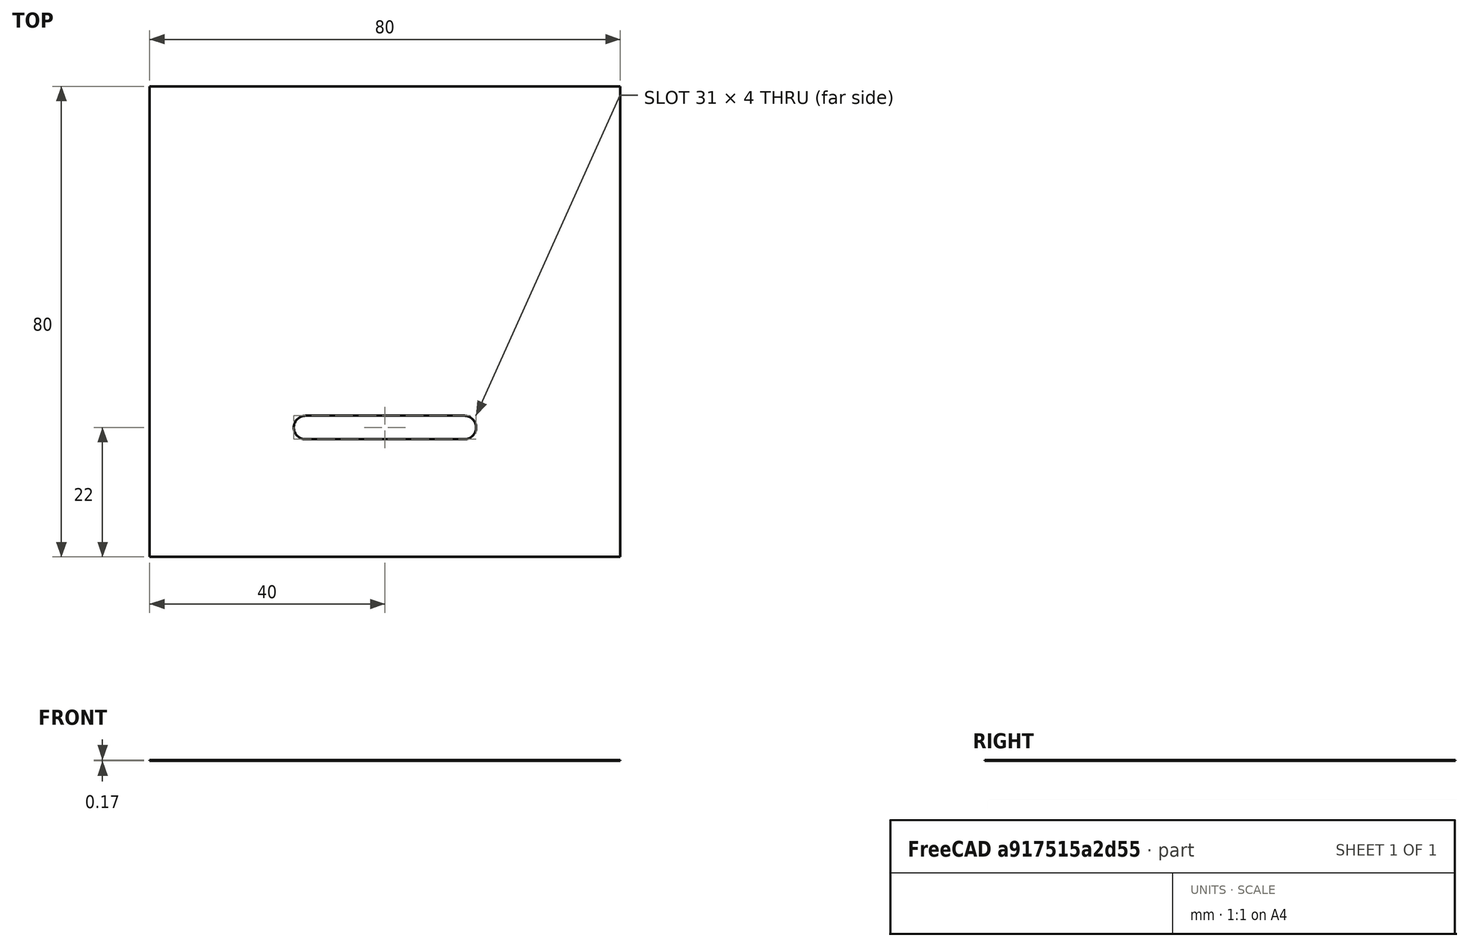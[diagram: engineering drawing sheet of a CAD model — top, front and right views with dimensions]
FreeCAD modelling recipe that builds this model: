
FCSTD DOCUMENT  (FreeCAD 0.19R24291 (Git))
Label: TopLabel
License: All rights reserved
LicenseURL: http://en.wikipedia.org/wiki/All_rights_reserved
objects: Part::Part2DObjectPython×3, Sketcher::SketchObject×2, Image::ImagePlane×1, PartDesign::Pad×1, PartDesign::Body×1
note: 8 computed .brp shape members not serialized (recipe doc carries the construction recipe); baked Part::Feature solids carry a one-line shape summary decoded from their .brp

FEATURE [Part::Part2DObjectPython] ShapeString  # Draft 2D object (typed FeaturePython)
  FontFile = <path>
  Placement = pos=(29.9,-64,0) rot=(0,0,1;0rad)
  Size = 3
  String = E0
  Tracking = 0
FEATURE [Part::Part2DObjectPython] ShapeString001  # Draft 2D object (typed FeaturePython)
  FontFile = <path>
  Placement = pos=(36.4,-64,0) rot=(0,0,1;0rad)
  Size = 3
  String = 2.4
  Tracking = 0
FEATURE [Part::Part2DObjectPython] ShapeString002  # Draft 2D object (typed FeaturePython)
  FontFile = <path>
  Placement = pos=(43.2,-64,0) rot=(0,0,1;0rad)
  Size = 3
  String = 5
  Tracking = 0
FEATURE [Sketcher::SketchObject] Sketch
  FullyConstrained = true
  MapMode = 5
  Support = -> [XY_Plane]
  sketch-geometry (9):
    g0: LineSegment StartX=0 StartY=0 StartZ=0 EndX=80 EndY=0 EndZ=0
    g1: LineSegment StartX=80 StartY=0 StartZ=0 EndX=80 EndY=-80 EndZ=0
    g2: LineSegment StartX=80 StartY=-80 StartZ=0 EndX=0 EndY=-80 EndZ=0
    g3: LineSegment StartX=0 StartY=-80 StartZ=0 EndX=0 EndY=0 EndZ=0
    g4: ArcOfCircle CenterX=26.5 CenterY=-58 CenterZ=0 NormalX=0 NormalY=0 NormalZ=1 AngleXU=0 Radius=2 StartAngle=1.5708 EndAngle=4.71239
    g5: ArcOfCircle CenterX=53.5 CenterY=-58 CenterZ=0 NormalX=0 NormalY=0 NormalZ=1 AngleXU=0 Radius=2 StartAngle=4.71239 EndAngle=7.85398
    g6: LineSegment StartX=26.5 StartY=-60 StartZ=0 EndX=53.5 EndY=-60 EndZ=0
    g7: LineSegment StartX=26.5 StartY=-56 StartZ=0 EndX=53.5 EndY=-56 EndZ=0
    g8: GeomPoint X=40 Y=-60 Z=0
  constraints (22):
    c: Coincident(g0,g1)
    c: Coincident(g1,g2)
    c: Coincident(g2,g3)
    c: Coincident(g3,g0)
    c: Horizontal(g0)
    c: Horizontal(g2)
    c: Vertical(g1)
    c: Vertical(g3)
    c: Coincident(g0,g-1)
    c: DistanceX(g0,g0) = 80
    c: DistanceY(g2,g0) = 80
    c: Tangent(g4,g7) = 1.5708
    c: Tangent(g4,g6) = -1.5708
    c: Tangent(g6,g5) = -1.5708
    c: Tangent(g7,g5) = 1.5708
    c: Horizontal(g6)
    c: Equal(g4,g5)
    c: DistanceY(g4,g4) = 4
    c: DistanceX(g4,g5) = 27
    c: Symmetric(g6,g6,g8)
    c: DistanceX(g0,g8) = 40
    c: DistanceY(g8,g0) = 60
FEATURE [Sketcher::SketchObject] MirroredSketch001
  FullyConstrained = false
  Placement = pos=(8,-51,0) rot=(0,0,1;0rad)
  sketch-geometry (86):
    g0: BSplineCurve PolesCount=2 KnotsCount=2 Degree=1 IsPeriodic=0
    g1: BSplineCurve PolesCount=2 KnotsCount=2 Degree=1 IsPeriodic=0
    g2: BSplineCurve PolesCount=2 KnotsCount=2 Degree=1 IsPeriodic=0
    g3: BSplineCurve PolesCount=4 KnotsCount=2 Degree=3 IsPeriodic=0
    g4: BSplineCurve PolesCount=2 KnotsCount=2 Degree=1 IsPeriodic=0
    g5: BSplineCurve PolesCount=4 KnotsCount=2 Degree=3 IsPeriodic=0
    g6: BSplineCurve PolesCount=2 KnotsCount=2 Degree=1 IsPeriodic=0
    g7: BSplineCurve PolesCount=4 KnotsCount=2 Degree=3 IsPeriodic=0
    g8: BSplineCurve PolesCount=2 KnotsCount=2 Degree=1 IsPeriodic=0
    g9: BSplineCurve PolesCount=4 KnotsCount=2 Degree=3 IsPeriodic=0
    g10: BSplineCurve PolesCount=2 KnotsCount=2 Degree=1 IsPeriodic=0
    g11: BSplineCurve PolesCount=2 KnotsCount=2 Degree=1 IsPeriodic=0
    g12: BSplineCurve PolesCount=2 KnotsCount=2 Degree=1 IsPeriodic=0
    g13: BSplineCurve PolesCount=4 KnotsCount=2 Degree=3 IsPeriodic=0
    g14: BSplineCurve PolesCount=4 KnotsCount=2 Degree=3 IsPeriodic=0
    g15: BSplineCurve PolesCount=2 KnotsCount=2 Degree=1 IsPeriodic=0
    g16: BSplineCurve PolesCount=2 KnotsCount=2 Degree=1 IsPeriodic=0
    g17: BSplineCurve PolesCount=2 KnotsCount=2 Degree=1 IsPeriodic=0
    g18: BSplineCurve PolesCount=4 KnotsCount=2 Degree=3 IsPeriodic=0
    g19: BSplineCurve PolesCount=2 KnotsCount=2 Degree=1 IsPeriodic=0
    g20: BSplineCurve PolesCount=4 KnotsCount=2 Degree=3 IsPeriodic=0
    g21: BSplineCurve PolesCount=2 KnotsCount=2 Degree=1 IsPeriodic=0
    g22: BSplineCurve PolesCount=4 KnotsCount=2 Degree=3 IsPeriodic=0
    g23: BSplineCurve PolesCount=2 KnotsCount=2 Degree=1 IsPeriodic=0
    g24: BSplineCurve PolesCount=4 KnotsCount=2 Degree=3 IsPeriodic=0
    g25: BSplineCurve PolesCount=2 KnotsCount=2 Degree=1 IsPeriodic=0
    g26: BSplineCurve PolesCount=2 KnotsCount=2 Degree=1 IsPeriodic=0
    g27: BSplineCurve PolesCount=2 KnotsCount=2 Degree=1 IsPeriodic=0
    g28: BSplineCurve PolesCount=2 KnotsCount=2 Degree=1 IsPeriodic=0
    g29: BSplineCurve PolesCount=2 KnotsCount=2 Degree=1 IsPeriodic=0
    g30: BSplineCurve PolesCount=4 KnotsCount=2 Degree=3 IsPeriodic=0
    g31: BSplineCurve PolesCount=2 KnotsCount=2 Degree=1 IsPeriodic=0
    g32: BSplineCurve PolesCount=4 KnotsCount=2 Degree=3 IsPeriodic=0
    g33: BSplineCurve PolesCount=2 KnotsCount=2 Degree=1 IsPeriodic=0
    g34: BSplineCurve PolesCount=4 KnotsCount=2 Degree=3 IsPeriodic=0
    g35: BSplineCurve PolesCount=2 KnotsCount=2 Degree=1 IsPeriodic=0
    g36: BSplineCurve PolesCount=4 KnotsCount=2 Degree=3 IsPeriodic=0
    g37: BSplineCurve PolesCount=2 KnotsCount=2 Degree=1 IsPeriodic=0
    g38: BSplineCurve PolesCount=2 KnotsCount=2 Degree=1 IsPeriodic=0
    g39: BSplineCurve PolesCount=2 KnotsCount=2 Degree=1 IsPeriodic=0
    g40: BSplineCurve PolesCount=4 KnotsCount=2 Degree=3 IsPeriodic=0
    g41: BSplineCurve PolesCount=4 KnotsCount=2 Degree=3 IsPeriodic=0
    g42: BSplineCurve PolesCount=4 KnotsCount=2 Degree=3 IsPeriodic=0
    g43: BSplineCurve PolesCount=4 KnotsCount=2 Degree=3 IsPeriodic=0
    g44: BSplineCurve PolesCount=4 KnotsCount=2 Degree=3 IsPeriodic=0
    g45: BSplineCurve PolesCount=4 KnotsCount=2 Degree=3 IsPeriodic=0
    g46: BSplineCurve PolesCount=4 KnotsCount=2 Degree=3 IsPeriodic=0
    g47: BSplineCurve PolesCount=4 KnotsCount=2 Degree=3 IsPeriodic=0
    g48: BSplineCurve PolesCount=4 KnotsCount=2 Degree=3 IsPeriodic=0
    g49: BSplineCurve PolesCount=4 KnotsCount=2 Degree=3 IsPeriodic=0
    g50: BSplineCurve PolesCount=4 KnotsCount=2 Degree=3 IsPeriodic=0
    g51: BSplineCurve PolesCount=4 KnotsCount=2 Degree=3 IsPeriodic=0
    g52: BSplineCurve PolesCount=4 KnotsCount=2 Degree=3 IsPeriodic=0
    g53: BSplineCurve PolesCount=4 KnotsCount=2 Degree=3 IsPeriodic=0
    g54: BSplineCurve PolesCount=4 KnotsCount=2 Degree=3 IsPeriodic=0
    g55: BSplineCurve PolesCount=4 KnotsCount=2 Degree=3 IsPeriodic=0
    g56: BSplineCurve PolesCount=4 KnotsCount=2 Degree=3 IsPeriodic=0
    g57: BSplineCurve PolesCount=4 KnotsCount=2 Degree=3 IsPeriodic=0
    g58: BSplineCurve PolesCount=4 KnotsCount=2 Degree=3 IsPeriodic=0
    g59: BSplineCurve PolesCount=4 KnotsCount=2 Degree=3 IsPeriodic=0
    g60: BSplineCurve PolesCount=4 KnotsCount=2 Degree=3 IsPeriodic=0
    g61: BSplineCurve PolesCount=4 KnotsCount=2 Degree=3 IsPeriodic=0
    g62: BSplineCurve PolesCount=4 KnotsCount=2 Degree=3 IsPeriodic=0
    g63: BSplineCurve PolesCount=4 KnotsCount=2 Degree=3 IsPeriodic=0
    g64: BSplineCurve PolesCount=4 KnotsCount=2 Degree=3 IsPeriodic=0
    g65: BSplineCurve PolesCount=4 KnotsCount=2 Degree=3 IsPeriodic=0
    g66: BSplineCurve PolesCount=4 KnotsCount=2 Degree=3 IsPeriodic=0
    g67: BSplineCurve PolesCount=4 KnotsCount=2 Degree=3 IsPeriodic=0
    g68: BSplineCurve PolesCount=4 KnotsCount=2 Degree=3 IsPeriodic=0
    g69: BSplineCurve PolesCount=4 KnotsCount=2 Degree=3 IsPeriodic=0
    g70: BSplineCurve PolesCount=4 KnotsCount=2 Degree=3 IsPeriodic=0
    g71: BSplineCurve PolesCount=4 KnotsCount=2 Degree=3 IsPeriodic=0
    g72: BSplineCurve PolesCount=4 KnotsCount=2 Degree=3 IsPeriodic=0
    g73: BSplineCurve PolesCount=4 KnotsCount=2 Degree=3 IsPeriodic=0
    g74: BSplineCurve PolesCount=4 KnotsCount=2 Degree=3 IsPeriodic=0
    g75: BSplineCurve PolesCount=4 KnotsCount=2 Degree=3 IsPeriodic=0
    g76: BSplineCurve PolesCount=4 KnotsCount=2 Degree=3 IsPeriodic=0
    g77: BSplineCurve PolesCount=4 KnotsCount=2 Degree=3 IsPeriodic=0
    g78: BSplineCurve PolesCount=4 KnotsCount=2 Degree=3 IsPeriodic=0
    g79: BSplineCurve PolesCount=4 KnotsCount=2 Degree=3 IsPeriodic=0
    g80: BSplineCurve PolesCount=4 KnotsCount=2 Degree=3 IsPeriodic=0
    g81: BSplineCurve PolesCount=4 KnotsCount=2 Degree=3 IsPeriodic=0
    g82: BSplineCurve PolesCount=4 KnotsCount=2 Degree=3 IsPeriodic=0
    g83: BSplineCurve PolesCount=4 KnotsCount=2 Degree=3 IsPeriodic=0
    g84: BSplineCurve PolesCount=4 KnotsCount=2 Degree=3 IsPeriodic=0
    g85: BSplineCurve PolesCount=4 KnotsCount=2 Degree=3 IsPeriodic=0
  constraints (86):
    c: Coincident(g0,g1)
    c: Coincident(g1,g2)
    c: Coincident(g2,g3)
    c: Coincident(g3,g4)
    c: Coincident(g4,g5)
    c: Coincident(g5,g6)
    c: Coincident(g6,g7)
    c: Coincident(g7,g8)
    c: Coincident(g8,g9)
    c: Coincident(g9,g10)
    c: Coincident(g10,g11)
    c: Coincident(g11,g12)
    c: Coincident(g12,g13)
    c: Coincident(g13,g14)
    c: Coincident(g14,g15)
    c: Coincident(g15,g16)
    c: Coincident(g16,g17)
    c: Coincident(g17,g18)
    c: Coincident(g18,g19)
    c: Coincident(g19,g20)
    c: Coincident(g20,g21)
    c: Coincident(g21,g22)
    c: Coincident(g22,g23)
    c: Coincident(g23,g24)
    c: Coincident(g24,g25)
    c: Coincident(g25,g26)
    c: Coincident(g26,g27)
    c: Coincident(g27,g28)
    c: Coincident(g28,g29)
    c: Coincident(g29,g30)
    c: Coincident(g30,g31)
    c: Coincident(g31,g32)
    c: Coincident(g32,g33)
    c: Coincident(g33,g34)
    c: Coincident(g34,g35)
    c: Coincident(g35,g36)
    c: Coincident(g36,g37)
    c: Coincident(g37,g38)
    c: Coincident(g38,g39)
    c: Coincident(g39,g40)
    c: Coincident(g40,g41)
    c: Coincident(g41,g0)
    c: Coincident(g42,g43)
    c: Coincident(g43,g44)
    c: Coincident(g44,g45)
    c: Coincident(g45,g46)
    c: Coincident(g46,g47)
    c: Coincident(g47,g42)
    c: Coincident(g48,g49)
    c: Coincident(g49,g50)
    c: Coincident(g50,g51)
    c: Coincident(g51,g48)
    c: Coincident(g52,g53)
    c: Coincident(g53,g54)
    c: Coincident(g54,g55)
    c: Coincident(g55,g56)
    c: Coincident(g56,g57)
    c: Coincident(g57,g52)
    c: Coincident(g58,g59)
    c: Coincident(g59,g60)
    c: Coincident(g60,g61)
    c: Coincident(g61,g62)
    c: Coincident(g62,g63)
    c: Coincident(g63,g58)
    c: Coincident(g64,g65)
    c: Coincident(g65,g66)
    c: Coincident(g66,g67)
    c: Coincident(g67,g68)
    c: Coincident(g68,g69)
    c: Coincident(g69,g64)
    c: Coincident(g70,g71)
    c: Coincident(g71,g72)
    c: Coincident(g72,g73)
    c: Coincident(g73,g70)
    c: Coincident(g74,g75)
    c: Coincident(g75,g76)
    c: Coincident(g76,g77)
    c: Coincident(g77,g78)
    c: Coincident(g78,g79)
    c: Coincident(g79,g74)
    c: Coincident(g80,g81)
    c: Coincident(g81,g82)
    c: Coincident(g82,g83)
    c: Coincident(g83,g84)
    c: Coincident(g84,g85)
    c: Coincident(g85,g80)
FEATURE [Image::ImagePlane] ImagePlane
  Placement = pos=(40,-20,0) rot=(0,0,1;0rad)
  XSize = 62.309
  YSize = 14.1761
FEATURE [PartDesign::Pad] Pad
  Direction = (1,1,1)
  Length = 0.175
  Length2 = 100
  Profile = -> Sketch
  Reversed = true
  Type = 0
FEATURE [PartDesign::Body] Body
  Group = -> [ShapeString,ShapeString001,ShapeString002,Sketch,MirroredSketch001,Pad]
  Origin = -> Origin
  Tip = -> Pad
note: 3 file-system paths scrubbed to <path> (originals preserved in the JSON sidecar)
